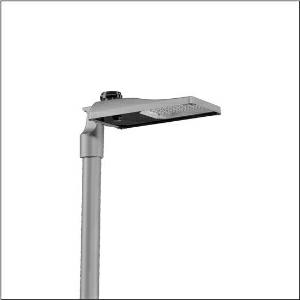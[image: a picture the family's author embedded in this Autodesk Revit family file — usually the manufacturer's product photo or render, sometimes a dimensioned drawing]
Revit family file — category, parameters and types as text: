
# Revit family: streetlight_sl_31_mini___st1_0a_5xh2d3bm08ha_2d93
name_source: partatom
category: Lighting Fixtures
units: mm (PartAtom-declared; Revit-internal decimal feet)

## family parameters
Cut with Voids When Loaded = No
Host = Face
Light Source = No
Part Type = Normal
Room Calculation Point = No
Round Connector Dimension = Use Diameter
Shared = No

## types (1)
- --- (1 x LED, 9230 lm, 68.3 W, 3000K)
    Apparent Load = 68 VA
    CIE Flux Codes = 37 72 97 100 100
    Color Rendering = 70
    Color Temperature = 3000K
    Default Elevation = 1800 mm
    Description = Streetlight SL 31 mini NEMA (7pin) mast luminaire for post-top, side-entry; light control with lens of PMMA; light distribution: ST1.0a, direct asymmetric distribution, for standard-compliant lighting for roads and squares; LED: luminous flux: 9.230lm, light colour: 730, colour temperature: 3000K; luminous efficacy: 135,3lm/W; control: pre-setting: linear dimming characteristic, flexible luminous flux parameterisation, time-dependent luminous flux control, constant luminous flux control, intelligent temperature release in ECG and LED module, overheat protection; luminaire housing, of diecast aluminium, Siteco® metallic grey (DB 702S), corrosivity category C5 high according to DIN EN ISO 12944; cover of toughened safety glass, transparent, mast flange of diecast aluminium, Siteco® metallic grey (DB 702S), spigot size: 76/60mm, mast flange included unmounted; with cable H07RN-F 3x 1.5mm², cable length: 8,5m, connection cable pre-assembled; mains connection: 220..240V, AC, 50/60Hz; power consumption (at start of service life): 68,2W / (at end of service life): 74,4W / (with reduced operation 50%): 29,7W; protection rating (complete): IP66; insulation class (complete): insulation class I (protective earthing); impact resistance: IK09; certification: CE, ENEC, ENEC+, VDE, UKCA; permissible operating ambient temperature for outdoor applications: -40..+50°C; packaging unit: 1 piece

Light Distribution: ST1.0a
    Height = 76 mm
    Lamp = 1 x LED
    Lamp Light Flux = 9230 lm
    Lamp Power = 68.3 W
    Lamp count = 1
    Length = 547 mm
    Luminous efficacy = 135 lm/W
    Manufacturer = Siteco
    ModVariant = No
    Model = 5XH2D3BM08HA
    Number of Poles = 1
    OnlyDefault = Yes
    Power Factor = 1
    Product Name = Streetlight SL 31 mini | ST1.0a
    Product group = mast luminaire | pylon top
    ProductGroupID = 6100
    Protection Class = Protection class I
    Protection Degree = IP 66
    RLX_Detail_Level = 1
    RLX_Emergency_Light_Flux = 0 lm
    RLX_Emergency_Type = 0
    RLX_Emergency_Type_DB = No
    RlxData = <blob elided: 24785 chars, md5=c28e64e6>
    Socket = socket
    Standby Power = 0 W
    System Light Flux = 9230 lm
    System Power = 68 W
    Type Comments = factory setting: luminous flux: 100 % | dim-lin: 254 | 692 mA
    Type Image = l_1300324.jpg
    URL = http://relux.com
    VarID = @adj_002653
    Voltage = 0 V
    Weight = 0.00 kg
    Width = 265 mm

## geometry (parser evidence)
native form markers: Blend x4, Sweep x11
no freeform markers — native parametric forms only
